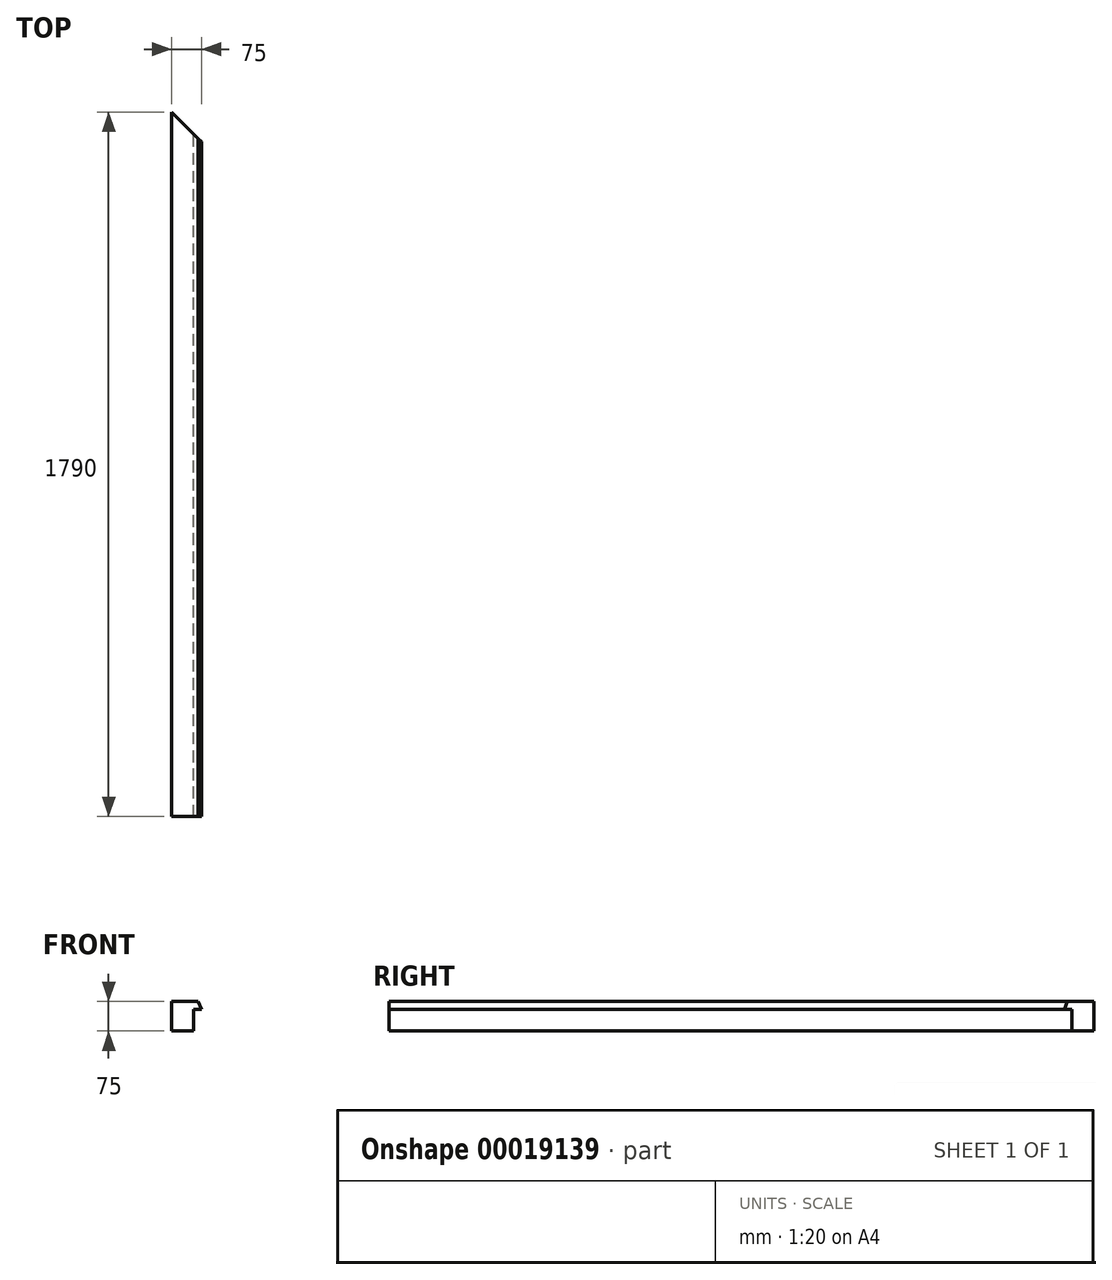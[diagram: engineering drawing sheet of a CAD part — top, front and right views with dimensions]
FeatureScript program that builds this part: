
annotation { "Feature Type Name" : "Feature", "Feature Type Description" : "" }
export const myFeature = defineFeature(function(context is Context, id is Id, definition is map)
    precondition{}
    {
        {
            var Q0;
            Q0=qCreatedBy(makeId("Front.planeOp"),FACE);
            var sketch = newSketch(context, id + "F0", { "sketchPlane" : qUnion([Q0])});
            skLineSegment(sketch, "E0.rect.bottom", {"start": v(17.5, -37.5) * mm, "end": v(-37.5, -37.5) * mm});
            skLineSegment(sketch, "E0.rect.top", {"start": v(29.5, 37.5) * mm, "end": v(-37.5, 37.5) * mm});
            skLineSegment(sketch, "E0.rect.right", {"start": v(-37.5, -37.5) * mm, "end": v(-37.5, 37.5) * mm});
            skPoint(sketch, "E0.rect.middle", {"position": v(0, 0) * mm});
            skLineSegment(sketch, "E1", {"start": v(17.5, -37.5) * mm, "end": v(17.5, 17.5) * mm});
            skLineSegment(sketch, "E2", {"start": v(17.5, 17.5) * mm, "end": v(37.5, 17.5) * mm});
            skLineSegment(sketch, "E3", {"start": v(37.5, 17.5) * mm, "end": v(29.5, 37.5) * mm});
            skPoint(sketch, "E4.orphan", {"position": v(37.5, 37.5) * mm});
            skPoint(sketch, "E5.orphan", {"position": v(37.5, -37.5) * mm});
            skSolve(sketch);
        }
        {
            var Q0;
            Q0 = qSketchRegion(id + "F0", true);
            extrude(context, id + "F1", {"entities" : qUnion([Q0]), "depth" : 1790 * mm});
        }
        {
            var Q0;
            Q0=makeQuery(id+"F1.opExtrude","SWEPT_FACE",FACE,{"disambiguationData":[OSD([sQuery(id+"F0.wireOp",EDGE,"E0.rect.top")])]});
            var sketch = newSketch(context, id + "F2", { "sketchPlane" : qUnion([Q0])});
            skLineSegment(sketch, "E6", {"start": v(-37.5, 0) * mm, "end": v(41.54, -79.04) * mm});
            skLineSegment(sketch, "E7", {"start": v(41.54, -79.04) * mm, "end": v(41.54, 0) * mm});
            skLineSegment(sketch, "E8", {"start": v(41.54, 0) * mm, "end": v(-37.5, 0) * mm});
            skSolve(sketch);
        }
        {
            var Q0;
            Q0 = qSketchRegion(id + "F2", true);
            extrude(context, id + "F3", {"entities" : qUnion([Q0]), "operationType" : NewBodyOperationType.REMOVE, "endBound" : BoundingType.THROUGH_ALL, "oppositeDirection" : true, "depth" : 25 * mm});
        }
    });
